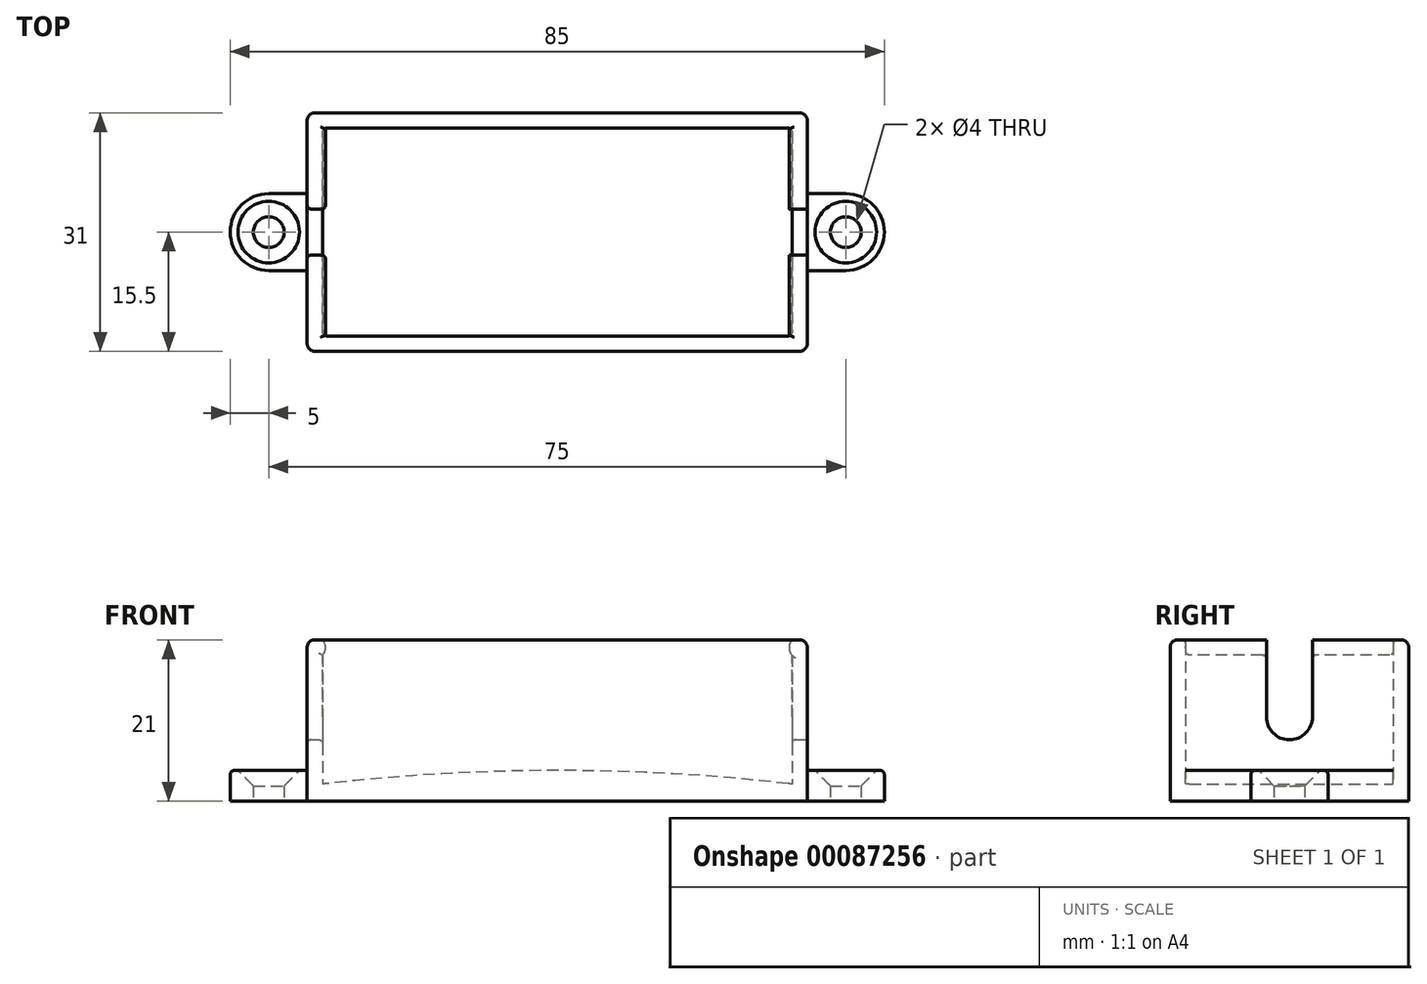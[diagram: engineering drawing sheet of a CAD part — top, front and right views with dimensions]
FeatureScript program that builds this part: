
annotation { "Feature Type Name" : "Feature", "Feature Type Description" : "" }
export const myFeature = defineFeature(function(context is Context, id is Id, definition is map)
    precondition{}
    {
        {
            var Q0;
            Q0=qCreatedBy(makeId("Top.planeOp"),FACE);
            var sketch = newSketch(context, id + "F0", { "sketchPlane" : qUnion([Q0])});
            skLineSegment(sketch, "E0.bottom", {"start": v(0, 0) * mm, "end": v(61, 0) * mm});
            skLineSegment(sketch, "E0.top", {"start": v(0, 27) * mm, "end": v(61, 27) * mm});
            skLineSegment(sketch, "E0.left", {"start": v(0, 0) * mm, "end": v(0, 27) * mm});
            skLineSegment(sketch, "E0.right", {"start": v(61, 0) * mm, "end": v(61, 27) * mm});
            skLineSegment(sketch, "E1.bottom", {"start": v(-2, -2) * mm, "end": v(63, -2) * mm});
            skLineSegment(sketch, "E1.top", {"start": v(-2, 29) * mm, "end": v(63, 29) * mm});
            skLineSegment(sketch, "E1.left", {"start": v(-2, -2) * mm, "end": v(-2, 29) * mm});
            skLineSegment(sketch, "E1.right", {"start": v(63, -2) * mm, "end": v(63, 29) * mm});
            skSolve(sketch);
        }
        {
            var Q0;
            Q0=qSketchRegion(id+"F0",true);
            extrude(context, id + "F1", {"entities" : qUnion([Q0]), "depth" : 21 * mm});
        }
        {
            var Q0;
            Q0=makeQuery(id+"F1.opExtrude","SWEPT_FACE",FACE,{"disambiguationData":[OSD([sQuery(id+"F0.wireOp",EDGE,"E1.top")])]});
            var sketch = newSketch(context, id + "F2", { "sketchPlane" : qUnion([Q0])});
            skLineSegment(sketch, "E2", {"start": v(-63, 0) * mm, "end": v(2, 0) * mm});
            skLineSegment(sketch, "E3", {"start": v(2, 0) * mm, "end": v(2, 2) * mm});
            skLineSegment(sketch, "E4", {"start": v(-63, 0) * mm, "end": v(-63, 2) * mm});
            skArc(sketch, "E5", {"start": v(2, 2) * mm, "mid": v(-30.5, 4) * mm, "end": v(-63, 2) * mm});
            skLineSegment(sketch, "E6", {"start": v(-30.5, 0) * mm, "end": v(-30.5, 6.8) * mm, "construction": true});
            skPoint(sketch, "E6.endSnap0", {"position": v(-30.5, 4) * mm});
            skSolve(sketch);
        }
        {
            var Q0;
            Q0=qSketchRegion(id+"F2",true);
            var Q1;
            Q1=makeQuery(id+"F1.opExtrude","SWEPT_FACE",FACE,{"disambiguationData":[OSD([sQuery(id+"F0.wireOp",EDGE,"E0.bottom")])]});
            extrude(context, id + "F3", {"entities" : qUnion([Q0]), "operationType" : NewBodyOperationType.ADD, "endBound" : BoundingType.UP_TO_SURFACE, "oppositeDirection" : true, "endBoundEntityFace" : qUnion([Q1]), "depth" : 25 * mm});
        }
        {
            var Q0;
            Q0=makeQuery(id+"F1.opExtrude","SWEPT_FACE",FACE,{"disambiguationData":[OSD([sQuery(id+"F0.wireOp",EDGE,"E0.bottom")])]});
            var sketch = newSketch(context, id + "F4", { "sketchPlane" : qUnion([Q0])});
            skArc(sketch, "E7", {"start": v(-61, 19) * mm, "mid": v(-60.62, 20) * mm, "end": v(-61, 21) * mm});
            skSolve(sketch);
        }
        {
            var Q0;
            Q0=qSketchRegion(id+"F4",true);
            var Q1;
            {var subQ0=sQuery(id+"F4.wireOp",EDGE,"E7");Q1=makeQuery(id+"F4.imprint","IMPRINT",FACE,{"disambiguationData":[TD([[makeQuery(id+"F4.imprint","IMPRINT",EDGE,{"derivedFrom":subQ0}),1.0]])]});}
            extrude(context, id + "F5", {"entities" : qUnion([Q0, Q1]), "operationType" : NewBodyOperationType.ADD, "endBound" : BoundingType.UP_TO_NEXT, "depth" : 25 * mm});
        }
        {
            var Q0;
            Q0=makeQuery(id+"F1.opExtrude","SWEPT_FACE",FACE,{"disambiguationData":[OSD([sQuery(id+"F0.wireOp",EDGE,"E0.bottom")])]});
            var sketch = newSketch(context, id + "F6", { "sketchPlane" : qUnion([Q0])});
            skArc(sketch, "E8", {"start": v(0, 21) * mm, "mid": v(-0.38, 20) * mm, "end": v(0, 19) * mm});
            skSolve(sketch);
        }
        {
            var Q0;
            Q0=qSketchRegion(id+"F6",true);
            var Q1;
            {var subQ0=sQuery(id+"F6.wireOp",EDGE,"E8");Q1=makeQuery(id+"F6.imprint","IMPRINT",FACE,{"disambiguationData":[TD([[makeQuery(id+"F6.imprint","IMPRINT",EDGE,{"derivedFrom":subQ0}),1.0]])]});}
            extrude(context, id + "F7", {"entities" : qUnion([Q0, Q1]), "operationType" : NewBodyOperationType.ADD, "endBound" : BoundingType.UP_TO_NEXT, "depth" : 25 * mm});
        }
        {
            var Q0;
            Q0=makeQuery(id+"F1.opExtrude","SWEPT_FACE",FACE,{"disambiguationData":[OSD([sQuery(id+"F0.wireOp",EDGE,"E1.right")])]});
            var sketch = newSketch(context, id + "F8", { "sketchPlane" : qUnion([Q0])});
            skLineSegment(sketch, "E9", {"start": v(10.5, 21) * mm, "end": v(10.5, 11) * mm});
            skLineSegment(sketch, "E10", {"start": v(16.5, 21) * mm, "end": v(16.5, 11) * mm});
            skArc(sketch, "E11", {"start": v(10.5, 11) * mm, "mid": v(13.5, 8) * mm, "end": v(16.5, 11) * mm});
            skSolve(sketch);
        }
        {
            var Q0;
            Q0=qSketchRegion(id+"F8",true);
            var Q1;
            {var subQ0=sQuery(id+"F8.wireOp",EDGE,"E9");Q1=makeQuery(id+"F8.imprint","IMPRINT",FACE,{"disambiguationData":[TD([[makeQuery(id+"F8.imprint","IMPRINT",EDGE,{"derivedFrom":subQ0}),1.0]])]});}
            extrude(context, id + "F9", {"entities" : qUnion([Q0, Q1]), "operationType" : NewBodyOperationType.REMOVE, "endBound" : BoundingType.THROUGH_ALL, "oppositeDirection" : true, "depth" : 25 * mm});
        }
        {
            var Q0;
            Q0=makeQuery(id+"F1.opExtrude","SWEPT_EDGE",EDGE,{"disambiguationData":[OSD([sQuery(id+"F0.wireOp",EDGE,"E0.bottom"),sQuery(id+"F0.wireOp",EDGE,"E0.right")])]});
            var Q1;
            Q1=makeQuery(id+"F1.opExtrude","SWEPT_EDGE",EDGE,{"disambiguationData":[OSD([sQuery(id+"F0.wireOp",EDGE,"E0.bottom"),sQuery(id+"F0.wireOp",EDGE,"E0.left")])]});
            var Q2;
            Q2=makeQuery(id+"F1.opExtrude","SWEPT_EDGE",EDGE,{"disambiguationData":[OSD([sQuery(id+"F0.wireOp",EDGE,"E0.top"),sQuery(id+"F0.wireOp",EDGE,"E0.left")])]});
            var Q3;
            Q3=makeQuery(id+"F1.opExtrude","SWEPT_EDGE",EDGE,{"disambiguationData":[OSD([sQuery(id+"F0.wireOp",EDGE,"E0.top"),sQuery(id+"F0.wireOp",EDGE,"E0.right")])]});
            fillet(context, id + "F10", {"entities" : qUnion([Q0, Q1, Q2, Q3]), "radius" : 0.5 * mm, "tangentPropagation" : true, "allowEdgeOverflow" : false});
        }
        {
            var Q0;
            Q0=makeQuery(id+"F1.opExtrude","SWEPT_EDGE",EDGE,{"disambiguationData":[OSD([sQuery(id+"F0.wireOp",EDGE,"E1.bottom"),sQuery(id+"F0.wireOp",EDGE,"E1.right")])]});
            var Q1;
            Q1=makeQuery(id+"F1.opExtrude","SWEPT_EDGE",EDGE,{"disambiguationData":[OSD([sQuery(id+"F0.wireOp",EDGE,"E1.top"),sQuery(id+"F0.wireOp",EDGE,"E1.right")])]});
            var Q2;
            Q2=makeQuery(id+"F1.opExtrude","SWEPT_EDGE",EDGE,{"disambiguationData":[OSD([sQuery(id+"F0.wireOp",EDGE,"E1.bottom"),sQuery(id+"F0.wireOp",EDGE,"E1.left")])]});
            var Q3;
            Q3=makeQuery(id+"F1.opExtrude","SWEPT_EDGE",EDGE,{"disambiguationData":[OSD([sQuery(id+"F0.wireOp",EDGE,"E1.top"),sQuery(id+"F0.wireOp",EDGE,"E1.left")])]});
            fillet(context, id + "F11", {"entities" : qUnion([Q0, Q1, Q2, Q3]), "radius" : 1 * mm, "tangentPropagation" : true, "allowEdgeOverflow" : false});
        }
        {
            var Q0;
            Q0=makeQuery(id+"F1.opExtrude","CAP_EDGE",EDGE,{"disambiguationData":[OSD([sQuery(id+"F0.wireOp",EDGE,"E1.bottom")])],"isStart":false});
            var Q1;
            Q1=makeQuery(id+"F1.opExtrude","CAP_EDGE",EDGE,{"disambiguationData":[OSD([sQuery(id+"F0.wireOp",EDGE,"E1.top")])],"isStart":false});
            fillet(context, id + "F12", {"entities" : qUnion([Q0, Q1]), "radius" : 1 * mm, "tangentPropagation" : true, "allowEdgeOverflow" : false});
        }
        {
            var Q0;
            Q0=makeQuery(id+"F1.opExtrude","CAP_EDGE",EDGE,{"disambiguationData":[OSD([sQuery(id+"F0.wireOp",EDGE,"E0.top")])],"isStart":false});
            var Q1;
            Q1=makeQuery(id+"F1.opExtrude","CAP_EDGE",EDGE,{"disambiguationData":[OSD([sQuery(id+"F0.wireOp",EDGE,"E0.bottom")])],"isStart":false});
            fillet(context, id + "F13", {"entities" : qUnion([Q0, Q1]), "radius" : 0.5 * mm, "tangentPropagation" : true, "allowEdgeOverflow" : false});
        }
        {
            var Q0;
            Q0=makeQuery(id+"F9.boolean.opBoolean","INTERSECT",EDGE,{"derivedFrom":[makeQuery(id+"F1.opExtrude","SWEPT_FACE",FACE,{"disambiguationData":[OSD([sQuery(id+"F0.wireOp",EDGE,"E0.left")])]}),makeQuery(id+"F9.opExtrude","SWEPT_FACE",FACE,{"disambiguationData":[OSD([sQuery(id+"F8.wireOp",EDGE,"E10")])]})]});
            var Q1;
            Q1=makeQuery(id+"F9.boolean.opBoolean","INTERSECT",EDGE,{"derivedFrom":[makeQuery(id+"F1.opExtrude","SWEPT_FACE",FACE,{"disambiguationData":[OSD([sQuery(id+"F0.wireOp",EDGE,"E1.left")])]}),makeQuery(id+"F9.opExtrude","SWEPT_FACE",FACE,{"disambiguationData":[OSD([sQuery(id+"F8.wireOp",EDGE,"E10")])]})]});
            var Q2;
            Q2=makeQuery(id+"F9.boolean.opBoolean","COPY",EDGE,{"derivedFrom":makeQuery(id+"F9.opExtrude","CAP_EDGE",EDGE,{"disambiguationData":[OSD([sQuery(id+"F8.wireOp",EDGE,"E10")])],"isStart":true})});
            var Q3;
            Q3=makeQuery(id+"F9.boolean.opBoolean","INTERSECT",EDGE,{"derivedFrom":[makeQuery(id+"F1.opExtrude","SWEPT_FACE",FACE,{"disambiguationData":[OSD([sQuery(id+"F0.wireOp",EDGE,"E0.right")])]}),makeQuery(id+"F9.opExtrude","SWEPT_FACE",FACE,{"disambiguationData":[OSD([sQuery(id+"F8.wireOp",EDGE,"E10")])]})]});
            fillet(context, id + "F14", {"entities" : qUnion([Q0, Q1, Q2, Q3]), "radius" : 0.5 * mm, "tangentPropagation" : true, "allowEdgeOverflow" : false});
        }
        {
            var Q0;
            Q0=makeQuery(id+"F3.boolean.opBoolean","MERGE",FACE,{"derivedFrom":[makeQuery(id+"F1.opExtrude","CAP_FACE",FACE,{"disambiguationData":[OSD([sQuery(id+"F0.wireOp",EDGE,"E0.bottom"),sQuery(id+"F0.wireOp",EDGE,"E0.top"),sQuery(id+"F0.wireOp",EDGE,"E0.left"),sQuery(id+"F0.wireOp",EDGE,"E0.right"),sQuery(id+"F0.wireOp",EDGE,"E1.bottom"),sQuery(id+"F0.wireOp",EDGE,"E1.top"),sQuery(id+"F0.wireOp",EDGE,"E1.left"),sQuery(id+"F0.wireOp",EDGE,"E1.right")])],"isStart":true}),makeQuery(id+"F3.opExtrude","SWEPT_FACE",FACE,{"disambiguationData":[OSD([sQuery(id+"F2.wireOp",EDGE,"E2")])]})]});
            var sketch = newSketch(context, id + "F15", { "sketchPlane" : qUnion([Q0])});
            skLineSegment(sketch, "E12", {"start": v(-2, -8.5) * mm, "end": v(-7, -8.5) * mm});
            skLineSegment(sketch, "E13", {"start": v(-7, -18.5) * mm, "end": v(-2, -18.5) * mm});
            skArc(sketch, "E14", {"start": v(-7, -8.5) * mm, "mid": v(-12, -13.5) * mm, "end": v(-7, -18.5) * mm});
            skCircle(sketch, "E15", {"center": v(-7, -13.5) * mm, "radius": 2 * mm});
            skLineSegment(sketch, "E16", {"start": v(30.5, 2) * mm, "end": v(30.5, -29) * mm, "construction": true});
            skLineSegment(sketch, "E17.MirrorCS", {"start": v(68, -18.5) * mm, "end": v(63, -18.5) * mm});
            skLineSegment(sketch, "E18.MirrorCS", {"start": v(63, -8.5) * mm, "end": v(68, -8.5) * mm});
            skArc(sketch, "E19.MirrorCS", {"start": v(68, -8.5) * mm, "mid": v(73, -13.5) * mm, "end": v(68, -18.5) * mm});
            skCircle(sketch, "E20.MirrorC", {"center": v(68, -13.5) * mm, "radius": 2 * mm});
            skSolve(sketch);
        }
        {
            var Q0;
            {var subQ1=sQuery(id+"F15.wireOp",EDGE,"E12");Q0=makeQuery(id+"F15.imprint","IMPRINT",FACE,{"disambiguationData":[TD([[makeQuery(id+"F15.imprint","IMPRINT",EDGE,{"derivedFrom":subQ1}),1.0]])]});}
            var Q1;
            {var subQ1=sQuery(id+"F15.wireOp",EDGE,"E17.MirrorCS");Q1=makeQuery(id+"F15.imprint","IMPRINT",FACE,{"disambiguationData":[TD([[makeQuery(id+"F15.imprint","IMPRINT",EDGE,{"derivedFrom":subQ1}),-1.0]])]});}
            extrude(context, id + "F16", {"entities" : qUnion([Q0, Q1]), "operationType" : NewBodyOperationType.ADD, "oppositeDirection" : true, "depth" : 4 * mm});
        }
        {
            var Q0;
            Q0=makeQuery(id+"F16.opExtrude","CAP_EDGE",EDGE,{"disambiguationData":[OSD([sQuery(id+"F15.wireOp",EDGE,"E15")])],"isStart":false});
            var Q1;
            Q1=makeQuery(id+"F16.opExtrude","CAP_EDGE",EDGE,{"disambiguationData":[OSD([sQuery(id+"F15.wireOp",EDGE,"E20.MirrorC")])],"isStart":false});
            chamfer(context, id + "F17", {"entities" : qUnion([Q0, Q1]), "width" : 2 * mm, "tangentPropagation" : true});
        }
        {
            var Q0;
            Q0=makeQuery(id+"F16.opExtrude","CAP_EDGE",EDGE,{"disambiguationData":[OSD([sQuery(id+"F15.wireOp",EDGE,"E14")])],"isStart":false});
            var Q1;
            Q1=makeQuery(id+"F16.opExtrude","CAP_EDGE",EDGE,{"disambiguationData":[OSD([sQuery(id+"F15.wireOp",EDGE,"E19.MirrorCS")])],"isStart":false});
            fillet(context, id + "F18", {"entities" : qUnion([Q0, Q1]), "radius" : 0.5 * mm, "tangentPropagation" : true, "allowEdgeOverflow" : false});
        }
    });
